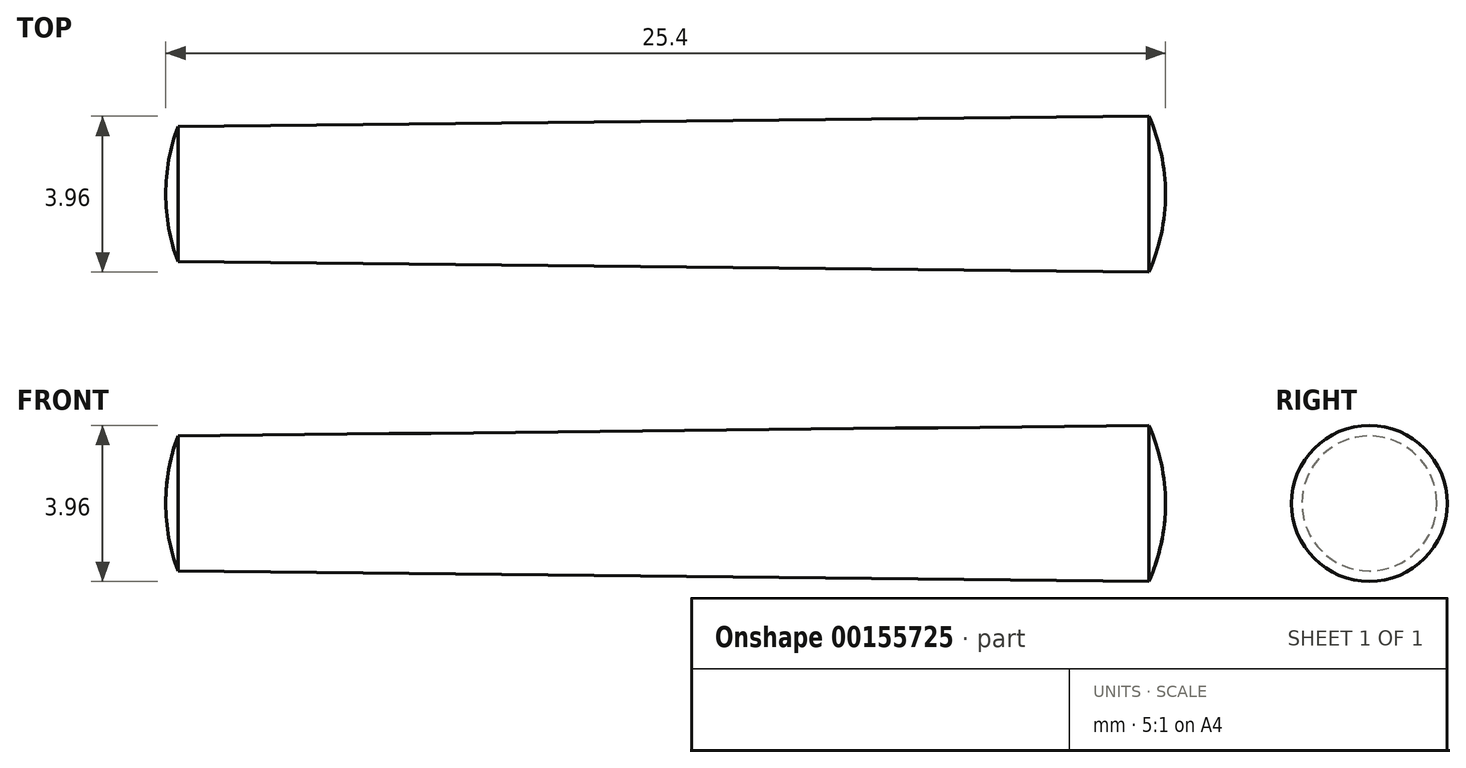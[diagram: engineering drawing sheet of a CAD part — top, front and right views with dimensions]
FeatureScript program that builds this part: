
annotation { "Feature Type Name" : "Feature", "Feature Type Description" : "" }
export const myFeature = defineFeature(function(context is Context, id is Id, definition is map)
    precondition{}
    {
        {
            var Q0;
            Q0=qCreatedBy(makeId("Front.planeOp"),FACE);
            var sketch = newSketch(context, id + "F1", { "sketchPlane" : qUnion([Q0])});
            skLineSegment(sketch, "E0", {"start": v(-12.39, 1.71) * mm, "end": v(12.28, 1.98) * mm});
            skArc(sketch, "E1", {"start": v(-12.39, 1.71) * mm, "mid": v(-12.62, 0.87) * mm, "end": v(-12.7, 0) * mm});
            skArc(sketch, "E2", {"start": v(12.7, 0) * mm, "mid": v(12.6, 1.01) * mm, "end": v(12.28, 1.98) * mm});
            skLineSegment(sketch, "E3", {"start": v(-12.7, 0) * mm, "end": v(12.7, 0) * mm});
            skSolve(sketch);
        }
        {
            var Q0;
            Q0 = qSketchRegion(id + "F1", true);
            var Q1;
            Q1=sQuery(id+"F1.wireOp",EDGE,"E3");
            revolve(context, id + "F0", {"entities" : qUnion([Q0]), "axis" : qUnion([Q1]), "revolveType" : RevolveType.FULL});
        }
    });
